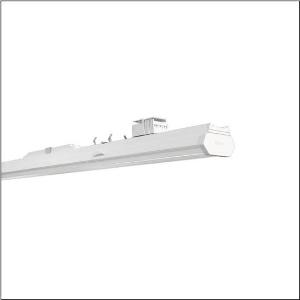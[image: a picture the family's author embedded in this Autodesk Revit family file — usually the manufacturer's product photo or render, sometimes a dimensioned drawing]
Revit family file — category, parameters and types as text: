
# Revit family: licross_r__11_protected_extreme_mo_51tp12dn495ge_fe34
name_source: partatom
category: Lighting Fixtures
units: mm (PartAtom-declared; Revit-internal decimal feet)

## family parameters
Cut with Voids When Loaded = No
Host = Face
Light Source = No
Part Type = Normal
Room Calculation Point = No
Round Connector Dimension = Use Diameter
Shared = No

## types (1)
- --- (1 x LED, 9980 lm, 57.1 W, 4000K)
    Apparent Load = 57 VA
    CIE Flux Codes = 73 92 98 99 100
    Color Rendering = 80
    Color Temperature = 4000K
    Default Elevation = 1800 mm
    Description = Licross® 11 Protected extreme MO, luminaire insert, of sheet steel, galvanised, coil coated, white, length: 1.500mm, width: 90mm, height: 101mm, LED rated luminous flux: 9.980lm, light colour: 840, control gear: DALI 2, with plug, 5-pole, with phase selection, mains connection: 220..240V, AC, 50/60Hz, rated input power: 57W, halogen-free wiring, primary optical cover: cover, of PMMA, light emission: direct distribution, primary light characteristic: symmetric, protection rating (complete): IP64, insulation class (complete): insulation class I (protective earthing), certification: CE, ENEC, VDE, UKCA, protection symbol: D if used in an environment with conductive dust loads with corresponding accessories, impact resistance: IK06, permissible ambient temperature for indoor applications: -40..+35°C, corresponds to IFS (International Featured Standards) requirements for safety and quality in the food industry, reducing of maximum allowable ambient temperature of 5°C with ceiling mounting, LABS conformity tested according to VDMA 24364:2018-05, packaging unit: 1 piece
    Height = 92 mm
    Lamp = 1 x LED
    Lamp Light Flux = 9980 lm
    Lamp Power = 57.1 W
    Lamp count = 1
    Length = 1500 mm
    Luminous efficacy = 175 lm/W
    Manufacturer = Siteco
    ModVariant = No
    Model = 51TP12DN495GE
    Mounting Place = Ceiling
    Mounting Type = Pendant
    Number of Poles = 1
    OnlyDefault = Yes
    Power Factor = 1
    Product Name = Licross® 11 Protected extreme MO
    Product group = luminaire insert
    ProductGroupID = 901
    Protection Class = Protection class I
    Protection Degree = IP 64
    RLX_Detail_Level = 1
    RLX_Emergency_Light_Flux = 0 lm
    RLX_Emergency_Type = 0
    RLX_Emergency_Type_DB = No
    RlxData = <blob elided: 24505 chars, md5=c49ef7e4>
    Socket = socket
    Standby Power = 0 W
    System Light Flux = 9980 lm
    System Power = 57 W
    Type Comments = factory setting: luminous flux: 100 % | dim-lin: 254 | 378 mA
    Type Image = l_1256148.jpg
    URL = http://relux.com
    VarID = @adj_051937
    Voltage = 0 V
    Weight = 0.00 kg
    Width = 88 mm

## geometry (parser evidence)
native form markers: Blend x4, Sweep x10
no freeform markers — native parametric forms only
